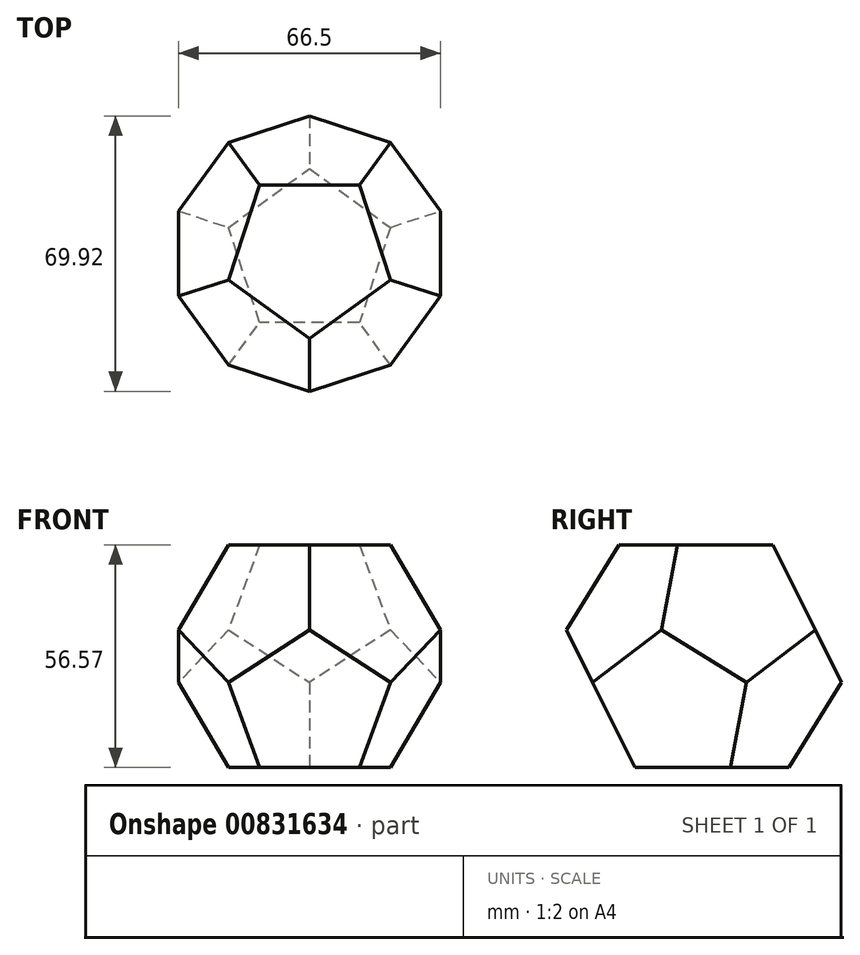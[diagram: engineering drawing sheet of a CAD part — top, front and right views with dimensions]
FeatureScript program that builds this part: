
annotation { "Feature Type Name" : "Feature", "Feature Type Description" : "" }
export const myFeature = defineFeature(function(context is Context, id is Id, definition is map)
    precondition{}
    {
        {
            var Q0;
            Q0=qCreatedBy(makeId("Top.planeOp"),FACE);
            var sketch = newSketch(context, id + "F0", { "sketchPlane" : qUnion([Q0])});
            skCircle(sketch, "E0.cCircle", {"center": v(0, 0) * mm, "radius": 17.48 * mm, "construction": true});
            skLineSegment(sketch, "E0.0", {"start": v(12.7, -17.48) * mm, "end": v(-12.7, -17.48) * mm});
            skLineSegment(sketch, "E0.1", {"start": v(-12.7, -17.48) * mm, "end": v(-20.55, 6.68) * mm});
            skLineSegment(sketch, "E0.2", {"start": v(-20.55, 6.68) * mm, "end": v(0, 21.6) * mm});
            skLineSegment(sketch, "E0.3", {"start": v(0, 21.6) * mm, "end": v(20.55, 6.68) * mm});
            skLineSegment(sketch, "E0.4", {"start": v(20.55, 6.68) * mm, "end": v(12.7, -17.48) * mm});
            skPoint(sketch, "E0.0.midPoint", {"position": v(0, -17.48) * mm});
            skSolve(sketch);
        }
        {
            var Q0;
            Q0=makeQuery(id+"F0.imprint","IMPRINT",FACE,{"disambiguationData":[TD([[makeQuery(id+"F0.imprint","IMPRINT",EDGE,{"derivedFrom":sQuery(id+"F0.wireOp",EDGE,"E0.0")}),-1.0]])]});
            extrude(context, id + "F1", {"entities" : qUnion([Q0]), "offsetDistance" : 25 * mm, "depth" : 25374.6 * mm, "hasDraft" : true, "draftAngle" : atan(2) / 2, "draftPullDirection" : true});
        }
        {
            var Q0;
            Q0=makeQuery(id+"F1.opExtrude","SWEPT_BODY",BODY,{"disambiguationData":[OSD([sQuery(id+"F0.wireOp",EDGE,"E0.0"),sQuery(id+"F0.wireOp",EDGE,"E0.1"),sQuery(id+"F0.wireOp",EDGE,"E0.2"),sQuery(id+"F0.wireOp",EDGE,"E0.3"),sQuery(id+"F0.wireOp",EDGE,"E0.4")])]});
            var Q1;
            Q1=makeQuery(id+"F1.opExtrude","SWEPT_EDGE",EDGE,{"disambiguationData":[OSD([sQuery(id+"F0.wireOp",EDGE,"E0.0"),sQuery(id+"F0.wireOp",EDGE,"E0.4")])]});
            circularPattern(context, id + "F2", {"operationType" : NewBodyOperationType.ADD, "entities" : qUnion([Q0]), "axis" : qUnion([Q1]), "angle" : 360 * degree, "instanceCount" : round(3), "equalSpace" : true});
        }
        {
            var Q0;
            Q0=makeQuery(id+"F1.opExtrude","SWEPT_BODY",BODY,{"disambiguationData":[OSD([sQuery(id+"F0.wireOp",EDGE,"E0.0"),sQuery(id+"F0.wireOp",EDGE,"E0.1"),sQuery(id+"F0.wireOp",EDGE,"E0.2"),sQuery(id+"F0.wireOp",EDGE,"E0.3"),sQuery(id+"F0.wireOp",EDGE,"E0.4")])]});
            var Q1;
            Q1=makeQuery(id+"F1.opExtrude","SWEPT_EDGE",EDGE,{"disambiguationData":[OSD([sQuery(id+"F0.wireOp",EDGE,"E0.1"),sQuery(id+"F0.wireOp",EDGE,"E0.2")])]});
            circularPattern(context, id + "F3", {"operationType" : NewBodyOperationType.ADD, "entities" : qUnion([Q0]), "axis" : qUnion([Q1]), "angle" : 360 * degree, "instanceCount" : round(3), "equalSpace" : true});
        }
        {
            var Q0;
            Q0=makeQuery(id+"F1.opExtrude","SWEPT_BODY",BODY,{"disambiguationData":[OSD([sQuery(id+"F0.wireOp",EDGE,"E0.0"),sQuery(id+"F0.wireOp",EDGE,"E0.1"),sQuery(id+"F0.wireOp",EDGE,"E0.2"),sQuery(id+"F0.wireOp",EDGE,"E0.3"),sQuery(id+"F0.wireOp",EDGE,"E0.4")])]});
            var Q1;
            Q1=makeQuery(id+"F2.opPattern","COPY",FACE,{"derivedFrom":makeQuery(id+"F1.opExtrude","SWEPT_FACE",FACE,{"disambiguationData":[OSD([sQuery(id+"F0.wireOp",EDGE,"E0.1")])]}),"instanceName":"2"});
            mirror(context, id + "F4", {"operationType" : NewBodyOperationType.ADD, "entities" : qUnion([Q0]), "mirrorPlane" : qUnion([Q1])});
        }
    });
